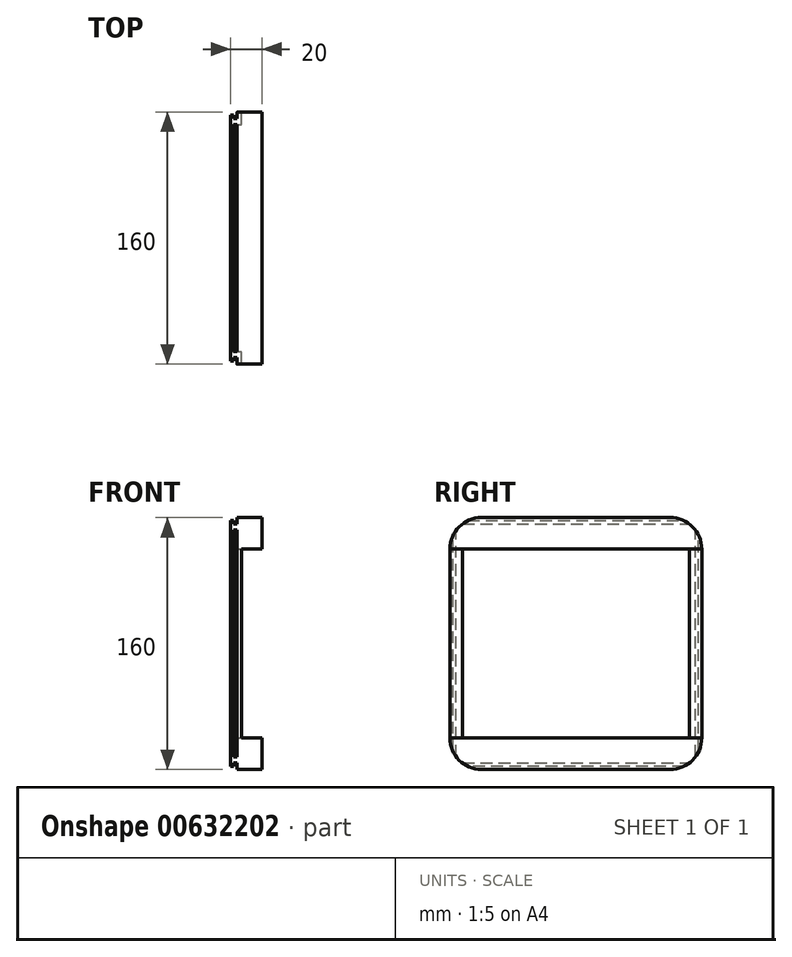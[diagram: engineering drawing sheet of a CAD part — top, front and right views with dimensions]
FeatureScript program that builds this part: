
annotation { "Feature Type Name" : "Feature", "Feature Type Description" : "" }
export const myFeature = defineFeature(function(context is Context, id is Id, definition is map)
    precondition{}
    {
        {
            var Q0;
            Q0=qCreatedBy(makeId("Right.planeOp"),FACE);
            var sketch = newSketch(context, id + "F0", { "sketchPlane" : qUnion([Q0])});
            skLineSegment(sketch, "E0.bottom", {"start": v(-52.85, -59.68) * mm, "end": v(107.15, -59.68) * mm});
            skLineSegment(sketch, "E0.top", {"start": v(-52.85, 100.32) * mm, "end": v(107.15, 100.32) * mm});
            skLineSegment(sketch, "E0.left", {"start": v(-52.85, -59.68) * mm, "end": v(-52.85, 100.32) * mm});
            skLineSegment(sketch, "E0.right", {"start": v(107.15, -59.68) * mm, "end": v(107.15, 100.32) * mm});
            skSolve(sketch);
        }
        {
            var Q0;
            Q0=makeQuery(id+"F0.imprint","IMPRINT",FACE,{"disambiguationData":[TD([[makeQuery(id+"F0.imprint","IMPRINT",EDGE,{"derivedFrom":sQuery(id+"F0.wireOp",EDGE,"E0.bottom")}),1.0]])]});
            extrude(context, id + "F1", {"entities" : qUnion([Q0]), "depth" : 20 * mm, "offsetDistance" : 25 * mm});
        }
        {
            var Q0;
            Q0=makeQuery(id+"F1.opExtrude","SWEPT_EDGE",EDGE,{"disambiguationData":[OSD([sQuery(id+"F0.wireOp",EDGE,"E0.top"),sQuery(id+"F0.wireOp",EDGE,"E0.left")])]});
            var Q1;
            Q1=makeQuery(id+"F1.opExtrude","SWEPT_EDGE",EDGE,{"disambiguationData":[OSD([sQuery(id+"F0.wireOp",EDGE,"E0.top"),sQuery(id+"F0.wireOp",EDGE,"E0.right")])]});
            var Q2;
            Q2=makeQuery(id+"F1.opExtrude","SWEPT_EDGE",EDGE,{"disambiguationData":[OSD([sQuery(id+"F0.wireOp",EDGE,"E0.bottom"),sQuery(id+"F0.wireOp",EDGE,"E0.left")])]});
            var Q3;
            Q3=makeQuery(id+"F1.opExtrude","SWEPT_EDGE",EDGE,{"disambiguationData":[OSD([sQuery(id+"F0.wireOp",EDGE,"E0.bottom"),sQuery(id+"F0.wireOp",EDGE,"E0.right")])]});
            fillet(context, id + "F2", {"entities" : qUnion([Q0, Q1, Q2, Q3]), "radius" : 20 * mm, "tangentPropagation" : true, "allowEdgeOverflow" : false});
        }
        {
            var Q0;
            Q0=makeQuery(id+"F1.opExtrude","CAP_FACE",FACE,{"disambiguationData":[OSD([sQuery(id+"F0.wireOp",EDGE,"E0.bottom"),sQuery(id+"F0.wireOp",EDGE,"E0.top"),sQuery(id+"F0.wireOp",EDGE,"E0.left"),sQuery(id+"F0.wireOp",EDGE,"E0.right")])],"isStart":false});
            var sketch = newSketch(context, id + "F3", { "sketchPlane" : qUnion([Q0])});
            skLineSegment(sketch, "E1.bottom", {"start": v(-44.85, 80.32) * mm, "end": v(99.15, 80.32) * mm});
            skLineSegment(sketch, "E1.top", {"start": v(-44.85, -39.68) * mm, "end": v(99.15, -39.68) * mm});
            skLineSegment(sketch, "E1.left", {"start": v(-44.85, 80.32) * mm, "end": v(-44.85, -39.68) * mm});
            skLineSegment(sketch, "E1.right", {"start": v(99.15, 80.32) * mm, "end": v(99.15, -39.68) * mm});
            skSolve(sketch);
        }
        {
            var Q0;
            Q0=makeQuery(id+"F3.imprint","IMPRINT",FACE,{"disambiguationData":[TD([[makeQuery(id+"F3.imprint","IMPRINT",EDGE,{"derivedFrom":sQuery(id+"F3.wireOp",EDGE,"E1.bottom")}),-1.0]])]});
            extrude(context, id + "F4", {"entities" : qUnion([Q0]), "operationType" : NewBodyOperationType.REMOVE, "oppositeDirection" : true, "depth" : 60 * mm, "offsetDistance" : 25 * mm});
        }
        {
            var Q0;
            Q0=makeQuery(id+"F1.opExtrude","CAP_FACE",FACE,{"disambiguationData":[OSD([sQuery(id+"F0.wireOp",EDGE,"E0.bottom"),sQuery(id+"F0.wireOp",EDGE,"E0.top"),sQuery(id+"F0.wireOp",EDGE,"E0.left"),sQuery(id+"F0.wireOp",EDGE,"E0.right")])],"isStart":false});
            var sketch = newSketch(context, id + "F5", { "sketchPlane" : qUnion([Q0])});
            skLineSegment(sketch, "E2.bottom", {"start": v(-52.85, 80.32) * mm, "end": v(107.15, 80.32) * mm});
            skLineSegment(sketch, "E2.top", {"start": v(-52.85, -39.68) * mm, "end": v(107.15, -39.68) * mm});
            skLineSegment(sketch, "E2.left", {"start": v(-52.85, 80.32) * mm, "end": v(-52.85, -39.68) * mm});
            skLineSegment(sketch, "E2.right", {"start": v(107.15, 80.32) * mm, "end": v(107.15, -39.68) * mm});
            skSolve(sketch);
        }
        {
            var Q0;
            Q0 = qSketchRegion(id + "F5", true);
            extrude(context, id + "F6", {"entities" : qUnion([Q0]), "operationType" : NewBodyOperationType.REMOVE, "oppositeDirection" : true, "depth" : 13 * mm, "offsetDistance" : 25 * mm});
        }
        {
            var Q0;
            Q0=makeQuery(id+"F1.opExtrude","SWEPT_FACE",FACE,{"disambiguationData":[OSD([sQuery(id+"F0.wireOp",EDGE,"E0.top")])]});
            var sketch = newSketch(context, id + "F7", { "sketchPlane" : qUnion([Q0])});
            skLineSegment(sketch, "E3.bottom", {"start": v(2, -57.7) * mm, "end": v(4, -57.7) * mm});
            skLineSegment(sketch, "E3.top", {"start": v(2, -48.85) * mm, "end": v(4, -48.85) * mm});
            skLineSegment(sketch, "E3.left", {"start": v(2, -57.7) * mm, "end": v(2, -48.85) * mm});
            skLineSegment(sketch, "E3.right", {"start": v(4, -57.7) * mm, "end": v(4, -48.85) * mm});
            skLineSegment(sketch, "E4.bottom", {"start": v(4, 103.15) * mm, "end": v(2, 103.15) * mm});
            skLineSegment(sketch, "E4.top", {"start": v(4, 113.7) * mm, "end": v(2, 113.7) * mm});
            skLineSegment(sketch, "E4.left", {"start": v(4, 103.15) * mm, "end": v(4, 113.7) * mm});
            skLineSegment(sketch, "E4.right", {"start": v(2, 103.15) * mm, "end": v(2, 113.7) * mm});
            skLineSegment(sketch, "E5.bottom", {"start": v(2, -50.85) * mm, "end": v(0, -50.85) * mm});
            skLineSegment(sketch, "E5.top", {"start": v(2, -52.85) * mm, "end": v(0, -52.85) * mm});
            skLineSegment(sketch, "E5.left", {"start": v(2, -50.85) * mm, "end": v(2, -52.85) * mm});
            skLineSegment(sketch, "E5.right", {"start": v(0, -50.85) * mm, "end": v(0, -52.85) * mm});
            skLineSegment(sketch, "E6.bottom", {"start": v(0, 107.15) * mm, "end": v(2, 107.15) * mm});
            skLineSegment(sketch, "E6.top", {"start": v(0, 105.15) * mm, "end": v(2, 105.15) * mm});
            skLineSegment(sketch, "E6.left", {"start": v(0, 107.15) * mm, "end": v(0, 105.15) * mm});
            skLineSegment(sketch, "E6.right", {"start": v(2, 107.15) * mm, "end": v(2, 105.15) * mm});
            skSolve(sketch);
        }
        {
            var Q0;
            Q0 = qSketchRegion(id + "F7", true);
            extrude(context, id + "F8", {"entities" : qUnion([Q0]), "operationType" : NewBodyOperationType.REMOVE, "oppositeDirection" : true, "depth" : 153.4 * mm, "offsetDistance" : 25 * mm});
        }
        {
            var Q0;
            {var subQ3=makeQuery(id+"F4.boolean.opBoolean","COPY",FACE,{"derivedFrom":makeQuery(id+"F4.opExtrude","SWEPT_FACE",FACE,{"disambiguationData":[OSD([sQuery(id+"F3.wireOp",EDGE,"E1.bottom")])]})});var subQ4=sQuery(id+"F0.wireOp",EDGE,"E0.right");var subQ9=makeQuery(id+"F1.opExtrude","SWEPT_FACE",FACE,{"disambiguationData":[OSD([subQ4])]});Q0=makeQuery(id+"F8.boolean.opBoolean","SPLIT",FACE,{"disambiguationData":[TD([subQ3])],"derivedFrom":subQ9});}
            var sketch = newSketch(context, id + "F9", { "sketchPlane" : qUnion([Q0])});
            skLineSegment(sketch, "E7.bottom", {"start": v(-2, 96.32) * mm, "end": v(-4, 96.32) * mm});
            skLineSegment(sketch, "E7.top", {"start": v(-2, 102.7) * mm, "end": v(-4, 102.7) * mm});
            skLineSegment(sketch, "E7.left", {"start": v(-2, 96.32) * mm, "end": v(-2, 102.7) * mm});
            skLineSegment(sketch, "E7.right", {"start": v(-4, 96.32) * mm, "end": v(-4, 102.7) * mm});
            skLineSegment(sketch, "E8.bottom", {"start": v(-2, -55.68) * mm, "end": v(-4, -55.68) * mm});
            skLineSegment(sketch, "E8.top", {"start": v(-2, -64.47) * mm, "end": v(-4, -64.47) * mm});
            skLineSegment(sketch, "E8.left", {"start": v(-2, -55.68) * mm, "end": v(-2, -64.47) * mm});
            skLineSegment(sketch, "E8.right", {"start": v(-4, -55.68) * mm, "end": v(-4, -64.47) * mm});
            skLineSegment(sketch, "E9.bottom", {"start": v(0, 100.32) * mm, "end": v(-2, 100.32) * mm});
            skLineSegment(sketch, "E9.top", {"start": v(0, 98.32) * mm, "end": v(-2, 98.32) * mm});
            skLineSegment(sketch, "E9.left", {"start": v(0, 100.32) * mm, "end": v(0, 98.32) * mm});
            skLineSegment(sketch, "E9.right", {"start": v(-2, 100.32) * mm, "end": v(-2, 98.32) * mm});
            skLineSegment(sketch, "E10.bottom", {"start": v(1.24, -60.47) * mm, "end": v(-2, -60.47) * mm});
            skLineSegment(sketch, "E10.top", {"start": v(1.24, -57.68) * mm, "end": v(-2, -57.68) * mm});
            skLineSegment(sketch, "E10.left", {"start": v(1.24, -60.47) * mm, "end": v(1.24, -57.68) * mm});
            skLineSegment(sketch, "E10.right", {"start": v(-2, -60.47) * mm, "end": v(-2, -57.68) * mm});
            skSolve(sketch);
        }
        {
            var Q0;
            Q0 = qSketchRegion(id + "F9", true);
            extrude(context, id + "F10", {"entities" : qUnion([Q0]), "operationType" : NewBodyOperationType.REMOVE, "depth" : -165 * mm, "offsetDistance" : 25 * mm});
        }
    });
